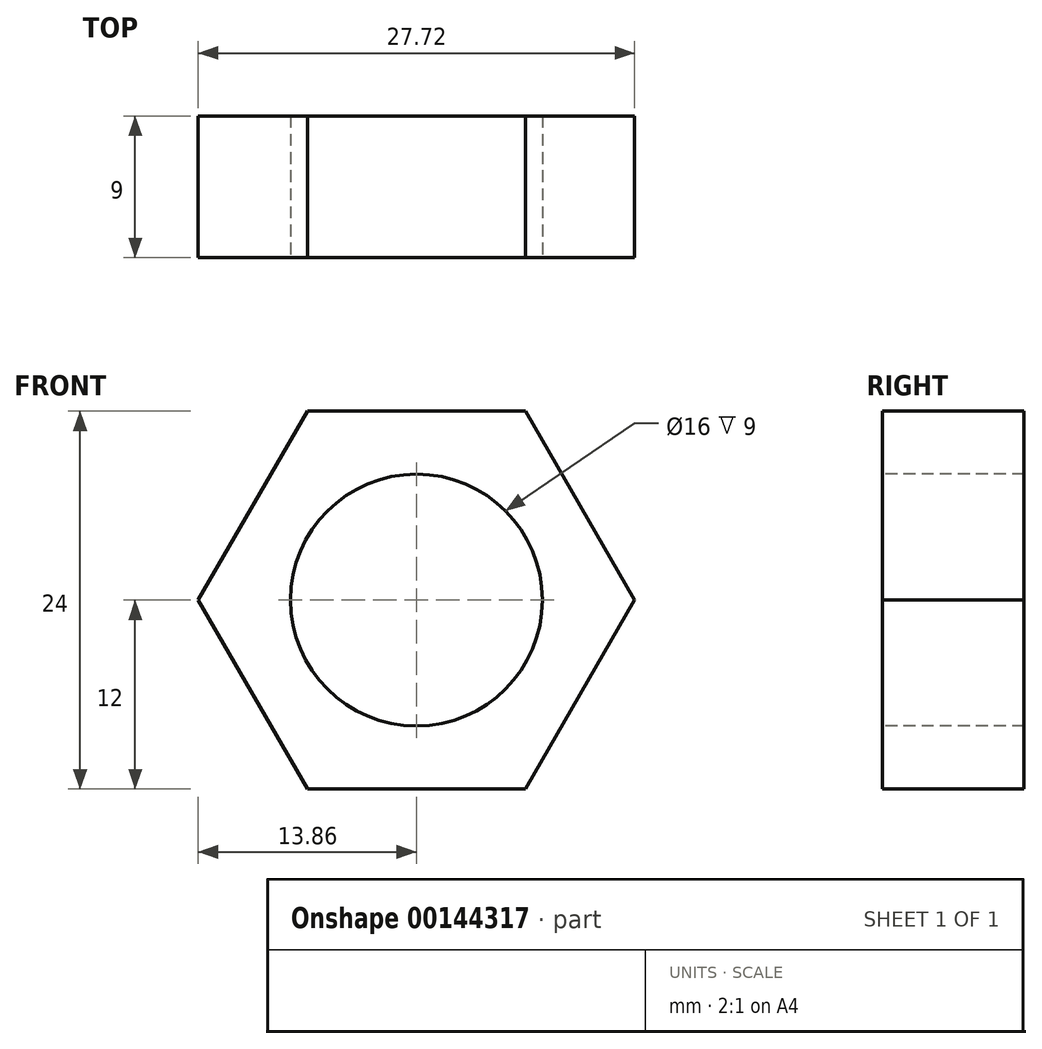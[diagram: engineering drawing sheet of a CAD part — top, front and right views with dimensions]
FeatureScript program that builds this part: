
annotation { "Feature Type Name" : "Feature", "Feature Type Description" : "" }
export const myFeature = defineFeature(function(context is Context, id is Id, definition is map)
    precondition{}
    {
        {
            var Q0;
            Q0=qCreatedBy(makeId("Front.planeOp"),FACE);
            var sketch = newSketch(context, id + "F0", { "sketchPlane" : qUnion([Q0])});
            skLineSegment(sketch, "E0", {"start": v(-6.93, 0) * mm, "end": v(6.93, 0) * mm});
            skLineSegment(sketch, "E1", {"start": v(6.93, 0) * mm, "end": v(13.86, 12) * mm});
            skLineSegment(sketch, "E2", {"start": v(13.86, 12) * mm, "end": v(6.93, 24) * mm});
            skLineSegment(sketch, "E3", {"start": v(6.93, 24) * mm, "end": v(-6.93, 24) * mm});
            skLineSegment(sketch, "E4", {"start": v(-6.93, 24) * mm, "end": v(-13.86, 12) * mm});
            skLineSegment(sketch, "E5", {"start": v(-13.86, 12) * mm, "end": v(-6.93, 0) * mm});
            skSolve(sketch);
        }
        {
            var Q0;
            Q0 = qSketchRegion(id + "F0", true);
            extrude(context, id + "F1", {"entities" : qUnion([Q0]), "depth" : 9 * mm});
        }
        {
            var Q0;
            Q0=makeQuery(id+"F1.opExtrude","CAP_FACE",FACE,{"disambiguationData":[OSD([sQuery(id+"F0.wireOp",EDGE,"E0"),sQuery(id+"F0.wireOp",EDGE,"E1"),sQuery(id+"F0.wireOp",EDGE,"E2"),sQuery(id+"F0.wireOp",EDGE,"E3"),sQuery(id+"F0.wireOp",EDGE,"E4"),sQuery(id+"F0.wireOp",EDGE,"E5")])],"isStart":false});
            var sketch = newSketch(context, id + "F2", { "sketchPlane" : qUnion([Q0])});
            skCircle(sketch, "E6", {"center": v(0, 12) * mm, "radius": 8 * mm});
            skSolve(sketch);
        }
        {
            var Q0;
            Q0 = qSketchRegion(id + "F2", true);
            extrude(context, id + "F3", {"entities" : qUnion([Q0]), "operationType" : NewBodyOperationType.REMOVE, "endBound" : BoundingType.THROUGH_ALL, "oppositeDirection" : true, "depth" : 25 * mm});
        }
    });
